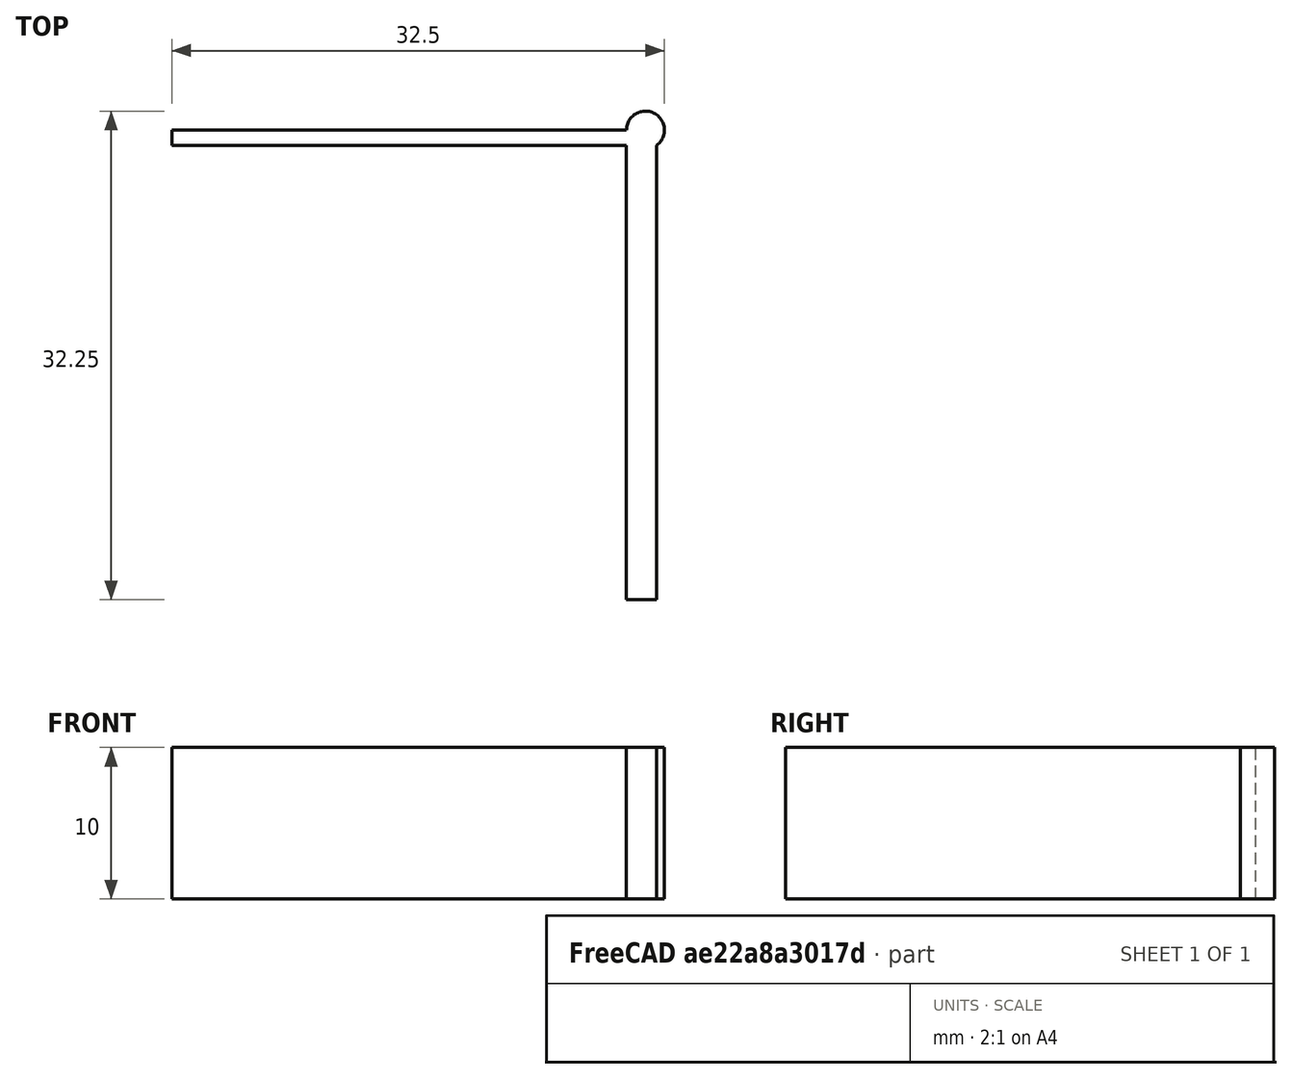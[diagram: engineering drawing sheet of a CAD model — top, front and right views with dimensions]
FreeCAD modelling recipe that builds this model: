
FCSTD DOCUMENT  (FreeCAD 0.20R29410 (Git))
Label: bar_spacer
License: All rights reserved
LicenseURL: http://en.wikipedia.org/wiki/All_rights_reserved
objects: Sketcher::SketchObject×1, PartDesign::Pad×1, PartDesign::Body×1
note: 4 computed .brp shape members not serialized (recipe doc carries the construction recipe); baked Part::Feature solids carry a one-line shape summary decoded from their .brp

FEATURE [Sketcher::SketchObject] Sketch
  FullyConstrained = true
  MapMode = 5
  Support = -> [XY_Plane]
  sketch-geometry (7):
    g0: LineSegment StartX=30 StartY=0 StartZ=0 EndX=30 EndY=30 EndZ=0
    g1: LineSegment StartX=30 StartY=30 StartZ=0 EndX=0 EndY=30 EndZ=0
    g2: LineSegment StartX=0 StartY=30 StartZ=0 EndX=0 EndY=31 EndZ=0
    g3: LineSegment StartX=0 StartY=31 StartZ=0 EndX=30 EndY=31 EndZ=0
    g4: LineSegment StartX=32 StartY=30 StartZ=0 EndX=32 EndY=0 EndZ=0
    g5: LineSegment StartX=32 StartY=0 StartZ=0 EndX=30 EndY=0 EndZ=0
    g6: ArcOfCircle CenterX=31.25 CenterY=31 CenterZ=0 NormalX=0 NormalY=0 NormalZ=1 AngleXU=0 Radius=1.25 StartAngle=5.35589 EndAngle=9.42478
  constraints (22):
    c: PointOnObject(g0,g-1)
    c: Vertical(g0)
    c: Coincident(g0,g1)
    c: PointOnObject(g1,g-2)
    c: Horizontal(g1)
    c: Coincident(g1,g2)
    c: PointOnObject(g2,g-2)
    c: Coincident(g2,g3)
    c: Horizontal(g3)
    c: Coincident(g4,g5)
    c: Coincident(g5,g0)
    c: Horizontal(g5)
    c: Vertical(g4)
    c: DistanceX(g1,g1) = 30
    c: DistanceY(g2,g2) = 1
    c: DistanceX(g5,g5) = 2
    c: Coincident(g3,g6)
    c: Coincident(g4,g6)
    c: Equal(g1,g0)
    c: Horizontal(g4,g0)
    c: Vertical(g3,g0)
    c: Radius(g6) = 1.25
FEATURE [PartDesign::Pad] Pad
  Direction = (0,0,1)
  Length = 10
  Length2 = 10
  Profile = -> Sketch
  ReferenceAxis = -> Sketch [N_Axis]
  Type = 0
FEATURE [PartDesign::Body] Body
  Group = -> [Sketch,Pad]
  Origin = -> Origin
  Tip = -> Pad
